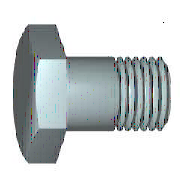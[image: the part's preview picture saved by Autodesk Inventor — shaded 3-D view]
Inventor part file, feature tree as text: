
AUTODESK INVENTOR PART (.ipt)
format: ipt  version: 2025 (Build 290162000, 162)  size: 196,608 bytes
history: native  units: mm (DEFAULTED — no unit token found)
features: other x1, extrude x1, chamfer x1, plane x1
ambient origin geometry x7: Origin, YZ Plane, XZ Plane, X Axis, Y Axis, Z Axis, Center Point
bodies: Solid1 (feature_tree)
feature tree (4):
  other  "轴承体"
  extrude  "头"  Depth=25.0mm
  chamfer  "倒角1"  Distance=23.5mm
  plane  "Work Plane1"
